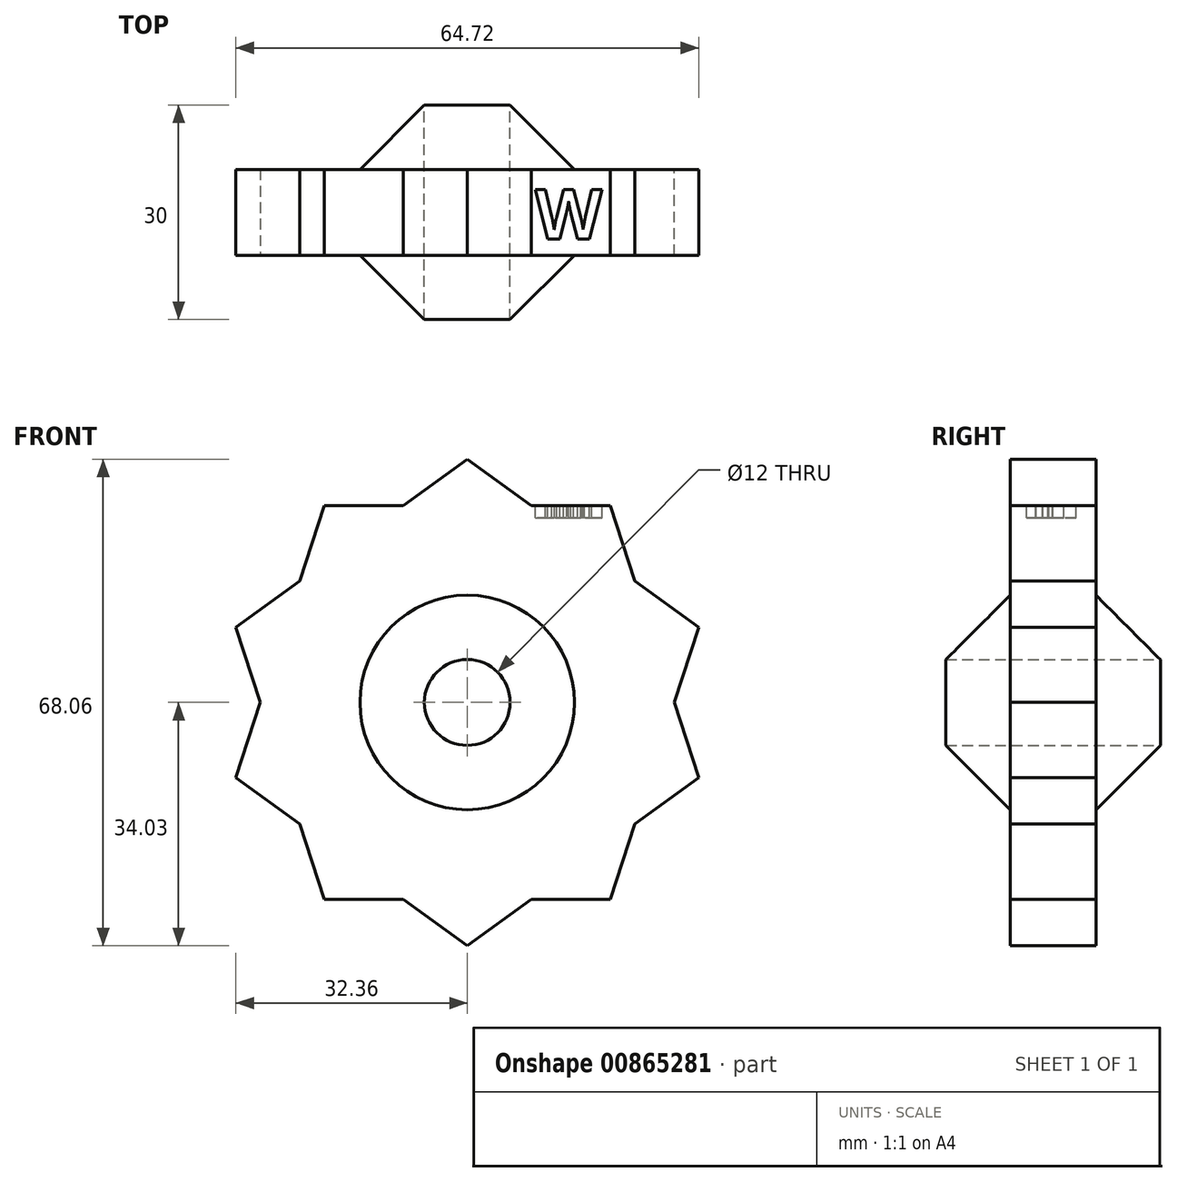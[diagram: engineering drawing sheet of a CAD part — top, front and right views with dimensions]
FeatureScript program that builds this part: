
annotation { "Feature Type Name" : "Feature", "Feature Type Description" : "" }
export const myFeature = defineFeature(function(context is Context, id is Id, definition is map)
    precondition{}
    {
        {
            var Q0;
            Q0=qCreatedBy(makeId("Front.planeOp"),FACE);
            var sketch = newSketch(context, id + "F0", { "sketchPlane" : qUnion([Q0])});
            skCircle(sketch, "E0.cCircle", {"center": v(0, 0) * mm, "radius": 27.53 * mm, "construction": true});
            skLineSegment(sketch, "E0.0", {"start": v(-20, 27.53) * mm, "end": v(20, 27.53) * mm});
            skLineSegment(sketch, "E0.1", {"start": v(20, 27.53) * mm, "end": v(32.36, -10.51) * mm});
            skLineSegment(sketch, "E0.2", {"start": v(32.36, -10.51) * mm, "end": v(0, -34.03) * mm});
            skLineSegment(sketch, "E0.3", {"start": v(0, -34.03) * mm, "end": v(-32.36, -10.51) * mm});
            skLineSegment(sketch, "E0.4", {"start": v(-32.36, -10.51) * mm, "end": v(-20, 27.53) * mm});
            skPoint(sketch, "E0.0.midPoint", {"position": v(0, 27.53) * mm});
            skSolve(sketch);
        }
        {
            var Q0;
            Q0=qCreatedBy(makeId("Front.planeOp"),FACE);
            var sketch = newSketch(context, id + "F1", { "sketchPlane" : qUnion([Q0])});
            skCircle(sketch, "E1.cCircle", {"center": v(0, 0) * mm, "radius": 34.03 * mm, "construction": true});
            skLineSegment(sketch, "E1.0", {"start": v(0, 34.03) * mm, "end": v(32.36, 10.51) * mm});
            skLineSegment(sketch, "E1.1", {"start": v(32.36, 10.51) * mm, "end": v(20, -27.53) * mm});
            skLineSegment(sketch, "E1.2", {"start": v(20, -27.53) * mm, "end": v(-20, -27.53) * mm});
            skLineSegment(sketch, "E1.3", {"start": v(-20, -27.53) * mm, "end": v(-32.36, 10.51) * mm});
            skLineSegment(sketch, "E1.4", {"start": v(-32.36, 10.51) * mm, "end": v(0, 34.03) * mm});
            skSolve(sketch);
        }
        {
            var Q0;
            Q0 = qSketchRegion(id + "F0", true);
            extrude(context, id + "F2", {"entities" : qUnion([Q0]), "depth" : 12 * mm, "offsetDistance" : 25 * mm});
        }
        {
            var Q0;
            Q0 = qSketchRegion(id + "F1", true);
            extrude(context, id + "F3", {"entities" : qUnion([Q0]), "operationType" : NewBodyOperationType.ADD, "depth" : 12 * mm, "offsetDistance" : 25 * mm});
        }
        {
            var Q0;
            Q0=makeQuery(id+"F3.boolean.opBoolean","MERGE",FACE,{"derivedFrom":[makeQuery(id+"F2.opExtrude","CAP_FACE",FACE,{"disambiguationData":[OSD([sQuery(id+"F0.wireOp",EDGE,"E0.0"),sQuery(id+"F0.wireOp",EDGE,"E0.1"),sQuery(id+"F0.wireOp",EDGE,"E0.2"),sQuery(id+"F0.wireOp",EDGE,"E0.3"),sQuery(id+"F0.wireOp",EDGE,"E0.4")])],"isStart":false}),makeQuery(id+"F3.opExtrude","CAP_FACE",FACE,{"disambiguationData":[OSD([sQuery(id+"F1.wireOp",EDGE,"E1.0"),sQuery(id+"F1.wireOp",EDGE,"E1.1"),sQuery(id+"F1.wireOp",EDGE,"E1.2"),sQuery(id+"F1.wireOp",EDGE,"E1.3"),sQuery(id+"F1.wireOp",EDGE,"E1.4")])],"isStart":false})]});
            var sketch = newSketch(context, id + "F4", { "sketchPlane" : qUnion([Q0])});
            skCircle(sketch, "E2", {"center": v(0, 0) * mm, "radius": 15 * mm});
            skSolve(sketch);
        }
        {
            var Q0;
            Q0=makeQuery(id+"F4.imprint","IMPRINT",FACE,{"disambiguationData":[TD([[makeQuery(id+"F4.imprint","IMPRINT",EDGE,{"derivedFrom":sQuery(id+"F4.wireOp",EDGE,"E2")}),1.0]])]});
            extrude(context, id + "F5", {"entities" : qUnion([Q0]), "operationType" : NewBodyOperationType.ADD, "depth" : 9 * mm, "offsetDistance" : 25 * mm});
        }
        {
            var Q0;
            Q0=makeQuery(id+"F3.boolean.opBoolean","MERGE",FACE,{"derivedFrom":[makeQuery(id+"F2.opExtrude","CAP_FACE",FACE,{"disambiguationData":[OSD([sQuery(id+"F0.wireOp",EDGE,"E0.0"),sQuery(id+"F0.wireOp",EDGE,"E0.1"),sQuery(id+"F0.wireOp",EDGE,"E0.2"),sQuery(id+"F0.wireOp",EDGE,"E0.3"),sQuery(id+"F0.wireOp",EDGE,"E0.4")])],"isStart":true}),makeQuery(id+"F3.opExtrude","CAP_FACE",FACE,{"disambiguationData":[OSD([sQuery(id+"F1.wireOp",EDGE,"E1.0"),sQuery(id+"F1.wireOp",EDGE,"E1.1"),sQuery(id+"F1.wireOp",EDGE,"E1.2"),sQuery(id+"F1.wireOp",EDGE,"E1.3"),sQuery(id+"F1.wireOp",EDGE,"E1.4")])],"isStart":true})]});
            var sketch = newSketch(context, id + "F6", { "sketchPlane" : qUnion([Q0])});
            skCircle(sketch, "E3", {"center": v(0, 0) * mm, "radius": 15 * mm});
            skSolve(sketch);
        }
        {
            var Q0;
            Q0=makeQuery(id+"F6.imprint","IMPRINT",FACE,{"disambiguationData":[TD([[makeQuery(id+"F6.imprint","IMPRINT",EDGE,{"derivedFrom":sQuery(id+"F6.wireOp",EDGE,"E3")}),1.0]])]});
            extrude(context, id + "F7", {"entities" : qUnion([Q0]), "operationType" : NewBodyOperationType.ADD, "depth" : 9 * mm, "offsetDistance" : 25 * mm});
        }
        {
            var Q0;
            Q0=makeQuery(id+"F7.opExtrude","CAP_FACE",FACE,{"disambiguationData":[OSD([sQuery(id+"F6.wireOp",EDGE,"E3")])],"isStart":false});
            chamfer(context, id + "F8", {"entities" : qUnion([Q0]), "width" : 9 * mm, "tangentPropagation" : true});
        }
        {
            var Q0;
            Q0=makeQuery(id+"F5.opExtrude","CAP_FACE",FACE,{"disambiguationData":[OSD([sQuery(id+"F4.wireOp",EDGE,"E2")])],"isStart":false});
            chamfer(context, id + "F9", {"entities" : qUnion([Q0]), "width" : 9 * mm, "tangentPropagation" : true});
        }
        {
            var Q0;
            Q0=makeQuery(id+"F7.opExtrude","CAP_FACE",FACE,{"disambiguationData":[OSD([sQuery(id+"F6.wireOp",EDGE,"E3")])],"isStart":false});
            var sketch = newSketch(context, id + "F10", { "sketchPlane" : qUnion([Q0])});
            skSolve(sketch);
        }
        {
            var Q0;
            {var subQ0=sQuery(id+"F6.wireOp",EDGE,"E3");Q0=makeQuery(id+"F10.imprint","IMPRINT",FACE,{"disambiguationData":[TD([[makeQuery(id+"F10.imprint","IMPRINT",EDGE,{"derivedFrom":makeQuery(id+"F8.opChamfer","BLEND_EDGE",EDGE,{"blendedFrom":[makeQuery(id+"F7.opExtrude","CAP_EDGE",EDGE,{"disambiguationData":[OSD([subQ0])],"isStart":false}),makeQuery(id+"F7.opExtrude","CAP_FACE",FACE,{"disambiguationData":[OSD([subQ0])],"isStart":false})],"blendedInto":[makeQuery(id+"F7.opExtrude","CAP_FACE",FACE,{"disambiguationData":[OSD([subQ0])],"isStart":false})]})}),1.0]])]});}
            extrude(context, id + "F11", {"entities" : qUnion([Q0]), "operationType" : NewBodyOperationType.REMOVE, "oppositeDirection" : true, "depth" : 90 * mm, "offsetDistance" : 25 * mm});
        }
        {
            var Q0;
            {var subQ0=sQuery(id+"F0.wireOp",EDGE,"E0.1");var subQ4=sQuery(id+"F0.wireOp",EDGE,"E0.0");Q0=makeQuery(id+"F3.boolean.opBoolean","SPLIT",FACE,{"disambiguationData":[TD([makeQuery(id+"F2.opExtrude","SWEPT_FACE",FACE,{"disambiguationData":[OSD([subQ0])]})])],"derivedFrom":makeQuery(id+"F2.opExtrude","SWEPT_FACE",FACE,{"disambiguationData":[OSD([subQ4])]})});}
            var sketch = newSketch(context, id + "F12", { "sketchPlane" : qUnion([Q0])});
            skText(sketch, "E4", { "text": "W", "fontName": "OpenSans-Bold.ttf"});
            const initialGuessF12  = {"E4": [0.0095, -0.00973, 1, 0, 0.00698]};
            skSetInitialGuess(sketch, initialGuessF12);
            skSolve(sketch);
        }
        {
            var Q0;
            Q0 = qSketchRegion(id + "F12", true);
            extrude(context, id + "F13", {"entities" : qUnion([Q0]), "operationType" : NewBodyOperationType.REMOVE, "oppositeDirection" : true, "depth" : 1.7 * mm, "offsetDistance" : 25 * mm});
        }
    });
